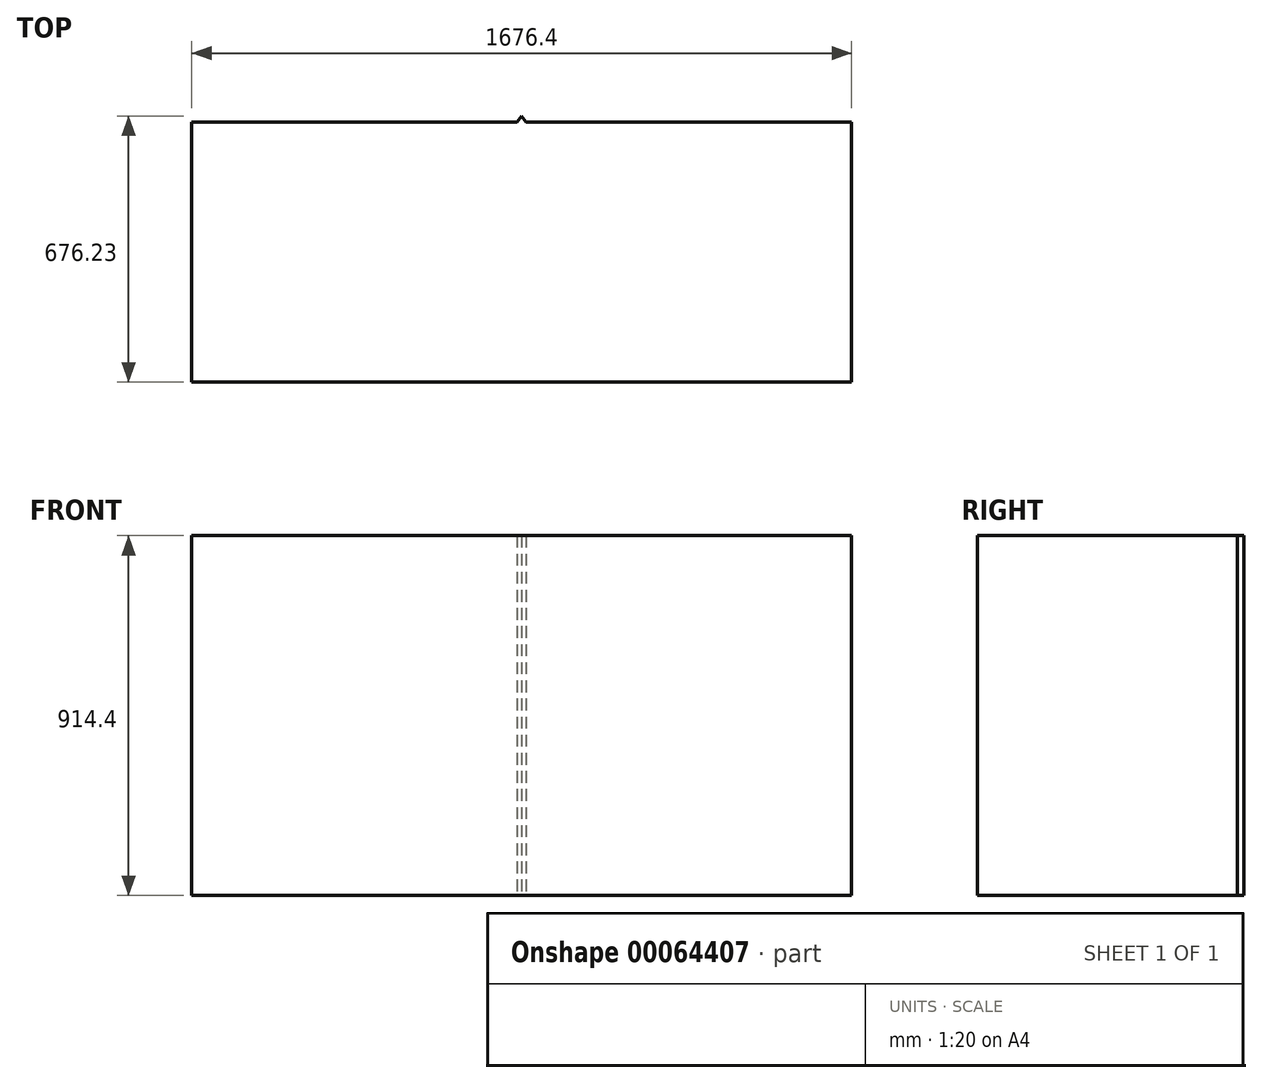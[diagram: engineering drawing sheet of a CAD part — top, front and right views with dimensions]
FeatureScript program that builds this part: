
annotation { "Feature Type Name" : "Feature", "Feature Type Description" : "" }
export const myFeature = defineFeature(function(context is Context, id is Id, definition is map)
    precondition{}
    {
        {
            var Q0;
            Q0=qCreatedBy(makeId("Top.planeOp"),FACE);
            var sketch = newSketch(context, id + "F0", { "sketchPlane" : qUnion([Q0])});
            skLineSegment(sketch, "E0.rect.bottom", {"start": v(-838.2, 330.2) * mm, "end": v(838.2, 330.2) * mm});
            skLineSegment(sketch, "E0.rect.top", {"start": v(-838.2, -330.2) * mm, "end": v(838.2, -330.2) * mm});
            skLineSegment(sketch, "E0.rect.left", {"start": v(-838.2, 330.2) * mm, "end": v(-838.2, -330.2) * mm});
            skLineSegment(sketch, "E0.rect.right", {"start": v(838.2, 330.2) * mm, "end": v(838.2, -330.2) * mm});
            skPoint(sketch, "E0.rect.middle", {"position": v(0, 0) * mm});
            skLineSegment(sketch, "E1", {"start": v(0, 330.2) * mm, "end": v(11.53, 330.2) * mm});
            skLineSegment(sketch, "E2", {"start": v(11.53, 330.2) * mm, "end": v(0, 346.03) * mm});
            skLineSegment(sketch, "E3", {"start": v(0, 346.03) * mm, "end": v(-11.52, 330.2) * mm});
            skLineSegment(sketch, "E4", {"start": v(-11.52, 330.2) * mm, "end": v(11.53, 330.2) * mm});
            skSolve(sketch);
        }
        {
            var Q0;
            Q0 = qSketchRegion(id + "F0", true);
            extrude(context, id + "F1", {"entities" : qUnion([Q0]), "depth" : 914.4 * mm});
        }
    });
